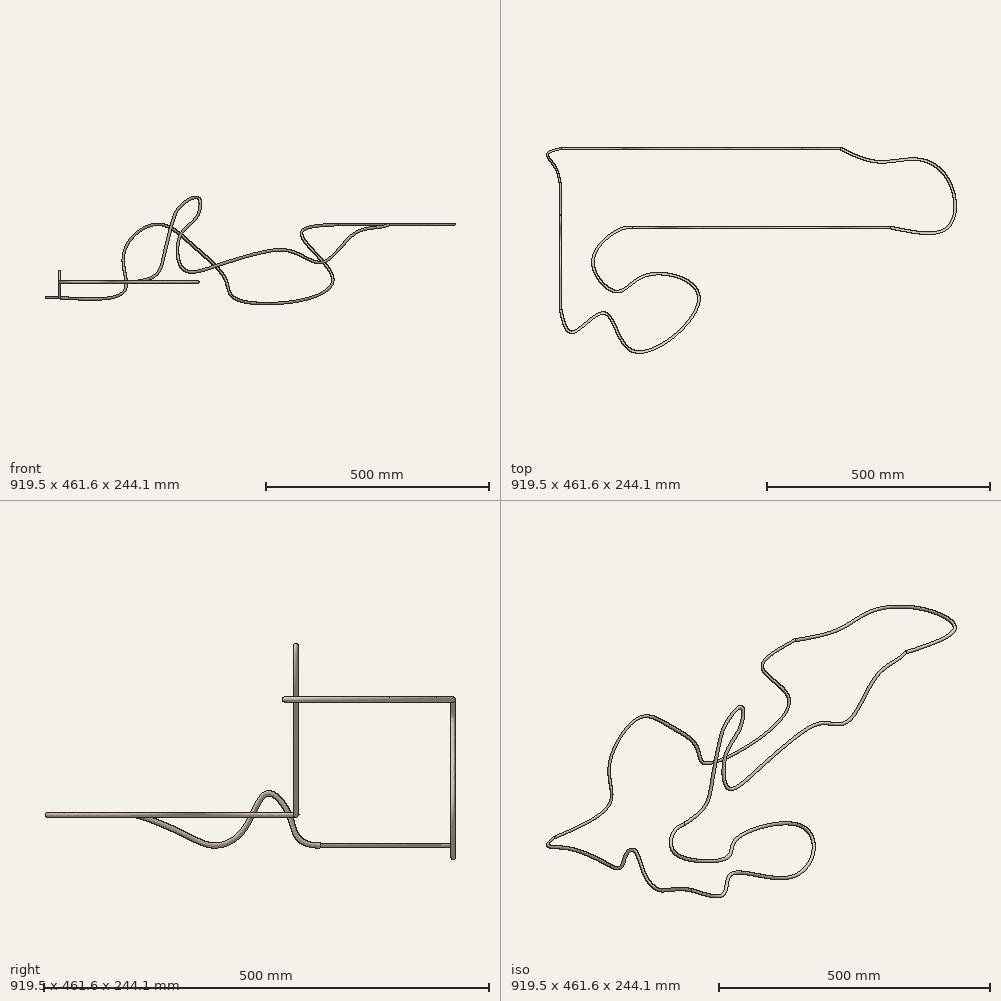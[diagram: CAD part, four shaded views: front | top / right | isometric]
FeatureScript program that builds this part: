
annotation { "Feature Type Name" : "Feature", "Feature Type Description" : "" }
export const myFeature = defineFeature(function(context is Context, id is Id, definition is map)
    precondition{}
    {
        {
            var Q0;
            Q0=qCreatedBy(makeId("Front.planeOp"),FACE);
            var sketch = newSketch(context, id + "F0", { "sketchPlane" : qUnion([Q0])});
            skCircle(sketch, "E0", {"center": v(0, 0) * mm, "radius": 3 * mm});
            skSolve(sketch);
        }
        {
            var Q0;
            Q0=qCreatedBy(makeId("Right.planeOp"),FACE);
            var sketch = newSketch(context, id + "F1", { "sketchPlane" : qUnion([Q0])});
            skFitSpline(sketch, "E1", {"points": [v(0, 0) * mm, v(-34.53, 32.9) * mm, v(-59.56, 58.43) * mm, v(-86.84, 16.46) * mm, v(-119.8, 0) * mm, v(-153.27, 12.85) * mm, v(-210.56, 34.7) * mm], "startDerivative": vector(-510.8, 0) * mm, "endDerivative": vector(-145.32, 9.72) * mm});
            skSolve(sketch);
        }
        {
            var Q0;
            Q0=makeQuery(id+"F0.imprint","IMPRINT",FACE,{"disambiguationData":[TD([[makeQuery(id+"F0.imprint","IMPRINT",EDGE,{"derivedFrom":sQuery(id+"F0.wireOp",EDGE,"E0")}),1.0]])]});
            var Q1;
            Q1=sQuery(id+"F1.wireOp",EDGE,"E1");
            sweep(context, id + "F2", {"profiles" : qUnion([Q0]), "path" : qUnion([Q1])});
        }
        {
            var Q0;
            Q0=sQuery(id+"F1.wireOp",VERTEX,"E1.end");
            var Q1;
            Q1=qCreatedBy(makeId("Top.planeOp"),FACE);
            cPlane(context, id + "F3", {"entities" : qUnion([Q0, Q1]), "cplaneType" : CPlaneType.PLANE_POINT, "offset" : 25 * mm, "width" : 150 * mm, "height" : 150 * mm});
        }
        {
            var Q0;
            Q0=qCreatedBy(id+"F3.planeOp",FACE);
            var sketch = newSketch(context, id + "F4", { "sketchPlane" : qUnion([Q0])});
            skPoint(sketch, "E2.0", {"position": v(0, -210.56) * mm});
            skFitSpline(sketch, "E3", {"points": [v(0, -210.56) * mm, v(27.43, -261.89) * mm, v(99.32, -219.4) * mm, v(164.02, -304.55) * mm, v(310.29, -184.5) * mm, v(194.44, -133.77) * mm, v(125.96, -170.72) * mm, v(72.77, -102.09) * mm, v(136.4, -30.72) * mm, v(161.88, -27.3) * mm], "startDerivative": vector(195.68, -896.8) * mm, "endDerivative": vector(350.58, -32.47) * mm});
            skSolve(sketch);
        }
        {
            var Q0;
            Q0=makeQuery(id+"F2.opSweep","CAP_FACE",FACE,{"disambiguationData":[OSD([sQuery(id+"F0.wireOp",EDGE,"E0"),sQuery(id+"F1.wireOp",VERTEX,"E1.end")])],"isStart":false});
            var Q1;
            Q1=sQuery(id+"F4.wireOp",EDGE,"E3");
            sweep(context, id + "F5", {"operationType" : NewBodyOperationType.ADD, "profiles" : qUnion([Q0]), "path" : qUnion([Q1])});
        }
        {
            var Q0;
            Q0=sQuery(id+"F4.wireOp",VERTEX,"E3.end");
            var Q1;
            Q1=qCreatedBy(makeId("Front.planeOp"),FACE);
            cPlane(context, id + "F6", {"entities" : qUnion([Q0, Q1]), "cplaneType" : CPlaneType.PLANE_POINT, "offset" : 25 * mm, "width" : 150 * mm, "height" : 150 * mm});
        }
        {
            var Q0;
            Q0=qCreatedBy(id+"F6.planeOp",FACE);
            var sketch = newSketch(context, id + "F7", { "sketchPlane" : qUnion([Q0])});
            skPoint(sketch, "E4.0", {"position": v(161.88, 34.7) * mm});
            skFitSpline(sketch, "E5", {"points": [v(161.88, 34.7) * mm, v(216.75, 51.16) * mm, v(236, 102.12) * mm, v(255.19, 174.9) * mm, v(271.44, 204.56) * mm, v(310.3, 223.84) * mm, v(308.27, 181.12) * mm, v(271.45, 139.97) * mm, v(277.45, 64.27) * mm, v(352.04, 71.47) * mm, v(459.7, 102.75) * mm, v(525.92, 101.83) * mm, v(592.04, 79.95) * mm, v(662.22, 143.5) * mm, v(721.54, 158.75) * mm, v(741.2, 164.4) * mm], "startDerivative": vector(988.94, 124.78) * mm, "endDerivative": vector(428.64, 170.38) * mm});
            skSolve(sketch);
        }
        {
            var Q0;
            Q0=makeQuery(id+"F5.opSweep","CAP_FACE",FACE,{"disambiguationData":[OSD([sQuery(id+"F0.wireOp",EDGE,"E0"),sQuery(id+"F1.wireOp",VERTEX,"E1.end"),sQuery(id+"F4.wireOp",VERTEX,"E3.end")])],"isStart":false});
            var Q1;
            Q1=sQuery(id+"F7.wireOp",EDGE,"E5");
            sweep(context, id + "F8", {"operationType" : NewBodyOperationType.ADD, "profiles" : qUnion([Q0]), "path" : qUnion([Q1])});
        }
        {
            var Q0;
            Q0=sQuery(id+"F7.wireOp",VERTEX,"E5.end");
            var Q1;
            Q1=qCreatedBy(makeId("Top.planeOp"),FACE);
            cPlane(context, id + "F9", {"entities" : qUnion([Q0, Q1]), "cplaneType" : CPlaneType.PLANE_POINT, "offset" : 25 * mm, "width" : 150 * mm, "height" : 150 * mm});
        }
        {
            var Q0;
            Q0=qCreatedBy(id+"F9.planeOp",FACE);
            var sketch = newSketch(context, id + "F10", { "sketchPlane" : qUnion([Q0])});
            skPoint(sketch, "E6.0", {"position": v(741.2, -27.3) * mm});
            skFitSpline(sketch, "E7", {"points": [v(741.2, -27.3) * mm, v(868.41, -27.3) * mm, v(876.03, 65.9) * mm, v(809.65, 124.67) * mm, v(714.99, 120.31) * mm, v(627.94, 149.7) * mm], "startDerivative": vector(682.61, -142.95) * mm, "endDerivative": vector(-438.2, 217.5) * mm});
            skSolve(sketch);
        }
        {
            var Q0;
            Q0=makeQuery(id+"F8.opSweep","CAP_FACE",FACE,{"disambiguationData":[OSD([sQuery(id+"F0.wireOp",EDGE,"E0"),sQuery(id+"F1.wireOp",VERTEX,"E1.end"),sQuery(id+"F4.wireOp",VERTEX,"E3.end"),sQuery(id+"F7.wireOp",VERTEX,"E5.end")])],"isStart":false});
            var Q1;
            Q1=sQuery(id+"F10.wireOp",EDGE,"E7");
            sweep(context, id + "F11", {"operationType" : NewBodyOperationType.ADD, "profiles" : qUnion([Q0]), "path" : qUnion([Q1])});
        }
        {
            var Q0;
            Q0=qCreatedBy(makeId("Front.planeOp"),FACE);
            var Q1;
            Q1=sQuery(id+"F10.wireOp",VERTEX,"E7.end");
            cPlane(context, id + "F12", {"entities" : qUnion([Q0, Q1]), "cplaneType" : CPlaneType.PLANE_POINT, "offset" : 25 * mm, "width" : 150 * mm, "height" : 150 * mm});
        }
        {
            var Q0;
            Q0=qCreatedBy(id+"F12.planeOp",FACE);
            var sketch = newSketch(context, id + "F13", { "sketchPlane" : qUnion([Q0])});
            skPoint(sketch, "E8.0", {"position": v(627.94, 164.4) * mm});
            skFitSpline(sketch, "E9", {"points": [v(627.94, 164.4) * mm, v(542.86, 142.8) * mm, v(611.12, 49.83) * mm, v(565.22, 0) * mm, v(391.05, 0) * mm, v(372.22, 40.42) * mm, v(295.73, 120.44) * mm, v(215.7, 164.4) * mm, v(143.92, 96.9) * mm, v(146.27, 15.7) * mm, v(0, 0) * mm], "startDerivative": vector(-1360.95, -56.41) * mm, "endDerivative": vector(-1625.7, 98.78) * mm});
            skSolve(sketch);
        }
        {
            var Q0;
            Q0=makeQuery(id+"F11.opSweep","CAP_FACE",FACE,{"disambiguationData":[OSD([sQuery(id+"F0.wireOp",EDGE,"E0"),sQuery(id+"F1.wireOp",VERTEX,"E1.end"),sQuery(id+"F4.wireOp",VERTEX,"E3.end"),sQuery(id+"F7.wireOp",VERTEX,"E5.end"),sQuery(id+"F10.wireOp",VERTEX,"E7.end")])],"isStart":false});
            var Q1;
            Q1=sQuery(id+"F13.wireOp",EDGE,"E9");
            sweep(context, id + "F14", {"operationType" : NewBodyOperationType.ADD, "profiles" : qUnion([Q0]), "path" : qUnion([Q1])});
        }
        {
            var Q0;
            Q0=sQuery(id+"F13.wireOp",VERTEX,"E9.end");
            var Q1;
            Q1=qCreatedBy(makeId("Top.planeOp"),FACE);
            cPlane(context, id + "F15", {"entities" : qUnion([Q0, Q1]), "cplaneType" : CPlaneType.PLANE_POINT, "offset" : 25 * mm, "width" : 150 * mm, "height" : 150 * mm});
        }
        {
            var Q0;
            Q0=qCreatedBy(id+"F15.planeOp",FACE);
            var sketch = newSketch(context, id + "F16", { "sketchPlane" : qUnion([Q0])});
            skPoint(sketch, "E10.0", {"position": v(0, 149.7) * mm});
            skFitSpline(sketch, "E11", {"points": [v(0, 149.7) * mm, v(-29.08, 136.88) * mm, v(-10.25, 105.1) * mm, v(0, 0) * mm], "startDerivative": vector(-161.5, -38.74) * mm, "endDerivative": vector(-8.87, -255.64) * mm});
            skSolve(sketch);
        }
        {
            var Q0;
            Q0=makeQuery(id+"F14.opSweep","CAP_FACE",FACE,{"disambiguationData":[OSD([sQuery(id+"F0.wireOp",EDGE,"E0"),sQuery(id+"F1.wireOp",VERTEX,"E1.end"),sQuery(id+"F4.wireOp",VERTEX,"E3.end"),sQuery(id+"F7.wireOp",VERTEX,"E5.end"),sQuery(id+"F10.wireOp",VERTEX,"E7.end"),sQuery(id+"F13.wireOp",VERTEX,"E9.end")])],"isStart":false});
            var Q1;
            Q1=sQuery(id+"F16.wireOp",EDGE,"E11");
            sweep(context, id + "F17", {"operationType" : NewBodyOperationType.ADD, "profiles" : qUnion([Q0]), "path" : qUnion([Q1])});
        }
    });
